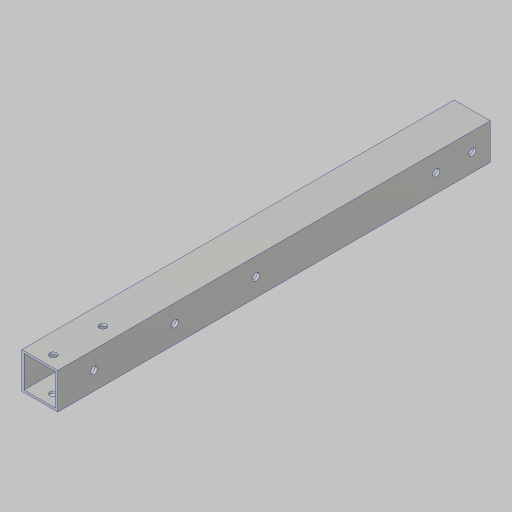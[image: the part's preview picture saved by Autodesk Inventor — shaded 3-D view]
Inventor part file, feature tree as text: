
AUTODESK INVENTOR PART (.ipt)
format: ipt  version: 2023.5 (Build 275446000, 446)  size: 134,144 bytes
history: native  units: in
note: dims shown in document units (in); Inventor stores cm internally (conversion verified against a paired STEP export)
features: hole x3, sketch x3, extrude x1, projected_geometry x1
ambient origin geometry x8: Origin, YZ Plane, XZ Plane, XY Plane, X Axis, Y Axis, Z Axis, Center Point
bodies: Solid1 (feature_tree)
feature tree (8):
  extrude  "Extrusion1"  Depth=0.5in
  hole  "Hole1"  [1 undecoded]
  hole  "Hole2"  [1 undecoded]
  hole  "Hole3"  [1 undecoded]
  sketch  "Sketch2"  dims[d4=0.0in d5=0.5in]
  sketch  "Sketch3"  dims[d6=1.0in]
  sketch  "Sketch4"  dims[d7=0.201in d8=0.75in d9=0.385in d10=0.25in d11=0.5635in d12=1.0in d13=0.8108in d14=1.375in d16=0.201in d17=0.75in d18=0.385in d19=0.25in d20=0.5635in d21=1.0in d22=0.8108in d23=1.0in d24=4.5in d25=0.201in d26=0.75in d27=0.375in d28=0.25in d29=0.5635in d30=1.0in d31=0.8108in d32=0.313in d33=0.0625in]
  projected_geometry  "Project Cut Edges1"
note: 3 required parameter values undecoded (feature->parameter linkage not recoverable at this tier; creation-order binding heuristic only, values carry confidence <= 0.55)
